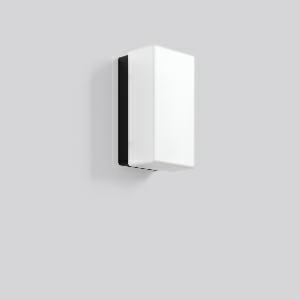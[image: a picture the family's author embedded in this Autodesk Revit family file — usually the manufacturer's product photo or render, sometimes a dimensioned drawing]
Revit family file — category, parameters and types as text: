
# Revit family: rechteck_20146_003_d4fe
name_source: partatom
category: Lighting Fixtures
units: mm (PartAtom-declared; Revit-internal decimal feet)

## family parameters
Cut with Voids When Loaded = No
Host = Face
Light Source = No
Part Type = Normal
Room Calculation Point = No
Round Connector Dimension = Use Diameter
Shared = No

## types (1)
- RECHTECK (1 x QA60/clear E27, 700 lm, 46 W, 3000)
    Apparent Load = 46 VA
    CIE Flux Codes = 34 63 85 72 42
    Color Rendering = 90
    Color Temperature = 3000
    Default Elevation = 1800 mm
    Description = Series: RECHTECK
Rectangular surface-mounted luminaire in classic design. Base: plastic. Opal glass: mouth blown, silk finish. Diffuser fastening: spring system. Suitable for Ceiling mounting, Wall (surface). IP 43 ceiling mounting, IP 44 wall mounting. 
Colour: black
Length: 220 mm
Width: 120 mm
Height: 105 mm
Lamp: A60
Number of lamps: 1
Wattage: 60 W
Socket: E27
System power: 46 W
Rated luminous flux: 300 lm
Luminous efficiency: 7 lm/W
Control gear: Converter not necessary
Protection class: II
Type of protection: IP 43
    Height = 105 mm
    Lamp = 1 x QA60/clear E27
    Lamp Light Flux = 700 lm
    Lamp Power = 46 W
    Lamp count = 1
    Length = 220 mm
    Lifetime = 3000 h
    Luminous efficacy = 6 lm/W
    Manufacturer = RZB
    ModVariant = No
    Model = 20146.003
    Mounting Place = Ceiling, Wall
    Mounting Type = Surface mounted
    Number of Poles = 1
    OnlyDefault = Yes
    Power Factor = 1
    Product Name = RECHTECK
    Product group = Surface mounted ceiling and wall luminaires
    ProductGroupID = 305
    Protection Class = Protection class II
    Protection Degree = IP 43
    RLX_Detail_Level = 1
    RLX_Emergency_Light_Flux = 0 lm
    RLX_Emergency_Type = 0
    RLX_Emergency_Type_DB = No
    RlxData = <blob elided: 20125 chars, md5=e9e32cb9>
    Socket = E27
    Standby Power = 0 W
    System Light Flux = 297 lm
    System Power = 46 W
    Type Comments = Product without accessories
    Type Image = 21146.003.jpg
    URL = http://relux.com
    VarID = ---
    Voltage = 230 V
    Voltage Range = 220-240 V
    Weight = 0.00 kg
    Width = 120 mm

## geometry (parser evidence)
native form markers: Blend x4, Sweep x14
no freeform markers — native parametric forms only
